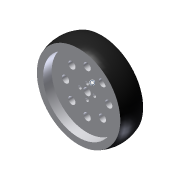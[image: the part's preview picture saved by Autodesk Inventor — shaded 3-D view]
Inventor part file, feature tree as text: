
AUTODESK INVENTOR PART (.ipt)
format: ipt  version: 2013 (Build 170138000, 138)  size: 156,160 bytes
history: native  units: in
note: dims shown in document units (in); Inventor stores cm internally (conversion verified against a paired STEP export)
features: other x1, imported_body x1, plane x1
ambient origin geometry x8: Origin, YZ Plane, XZ Plane, XY Plane, X Axis, Y Axis, Z Axis, Center Point
feature tree (3):
  other  "WHEEL_101MM_4-IN_2011"
  imported_body  "Base1"
  plane  "Work Plane1"
